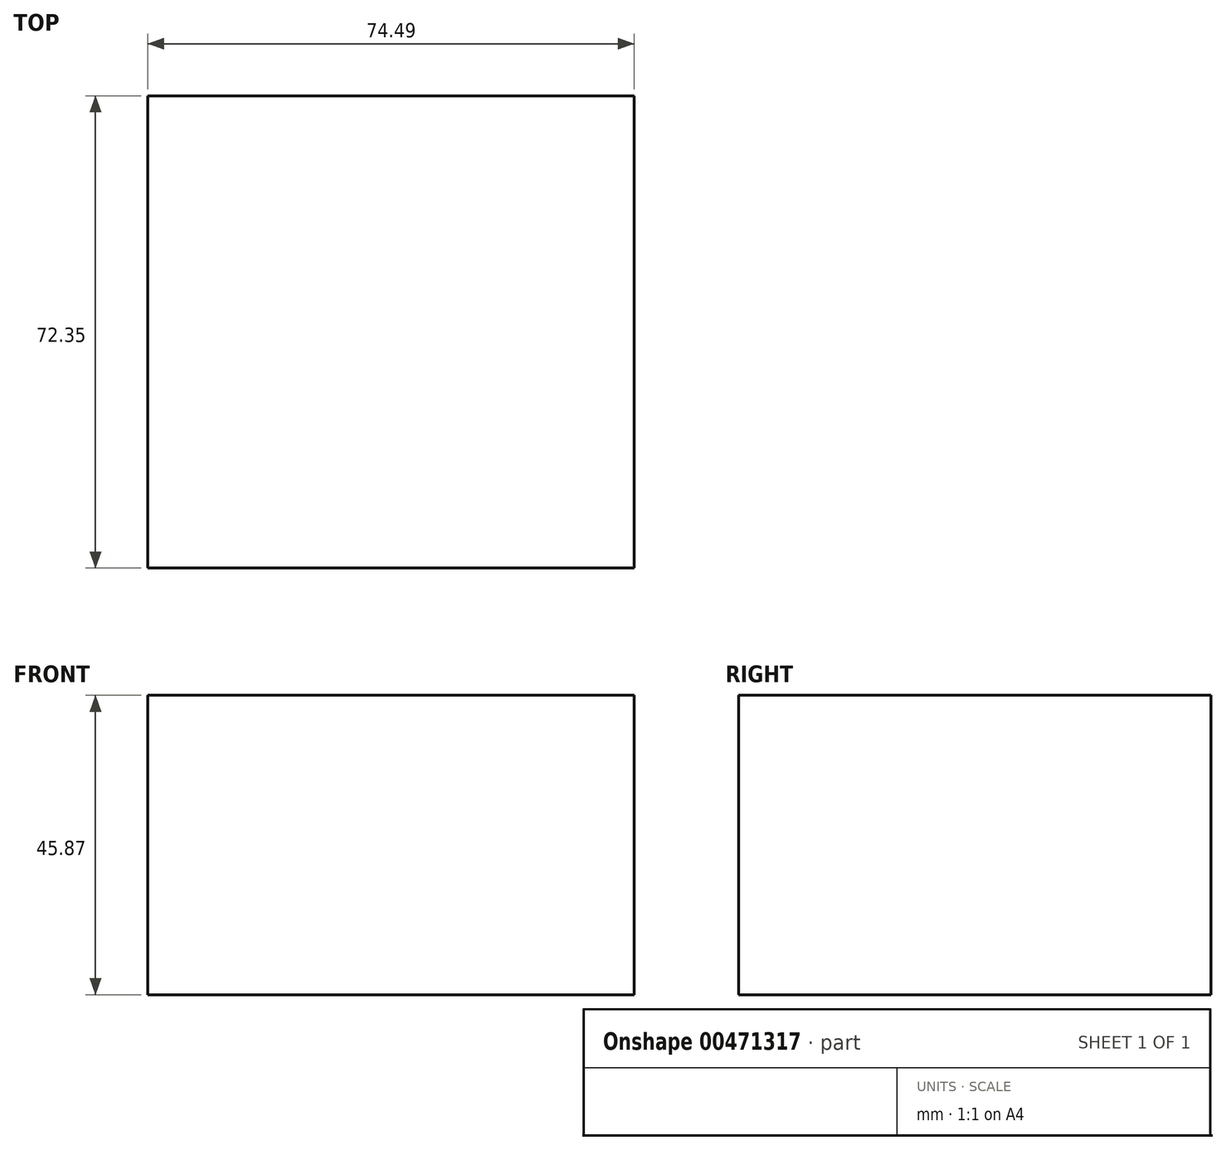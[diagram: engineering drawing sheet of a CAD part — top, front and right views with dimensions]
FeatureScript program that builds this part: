
annotation { "Feature Type Name" : "Feature", "Feature Type Description" : "" }
export const myFeature = defineFeature(function(context is Context, id is Id, definition is map)
    precondition{}
    {
        {
            var Q0;
            Q0=qCreatedBy(makeId("Top.planeOp"),FACE);
            var sketch = newSketch(context, id + "F0", { "sketchPlane" : qUnion([Q0])});
            skLineSegment(sketch, "E0.bottom", {"start": v(-42.92, 52) * mm, "end": v(31.57, 52) * mm});
            skLineSegment(sketch, "E0.top", {"start": v(-42.92, -20.35) * mm, "end": v(31.57, -20.35) * mm});
            skLineSegment(sketch, "E0.left", {"start": v(-42.92, 52) * mm, "end": v(-42.92, -20.35) * mm});
            skLineSegment(sketch, "E0.right", {"start": v(31.57, 52) * mm, "end": v(31.57, -20.35) * mm});
            skSolve(sketch);
        }
        {
            var Q0;
            Q0=makeQuery(id+"F0.imprint","IMPRINT",FACE,{"disambiguationData":[TD([[makeQuery(id+"F0.imprint","IMPRINT",EDGE,{"derivedFrom":sQuery(id+"F0.wireOp",EDGE,"E0.bottom")}),-1.0]])]});
            extrude(context, id + "F1", {"entities" : qUnion([Q0]), "depth" : 45.87 * mm});
        }
    });
